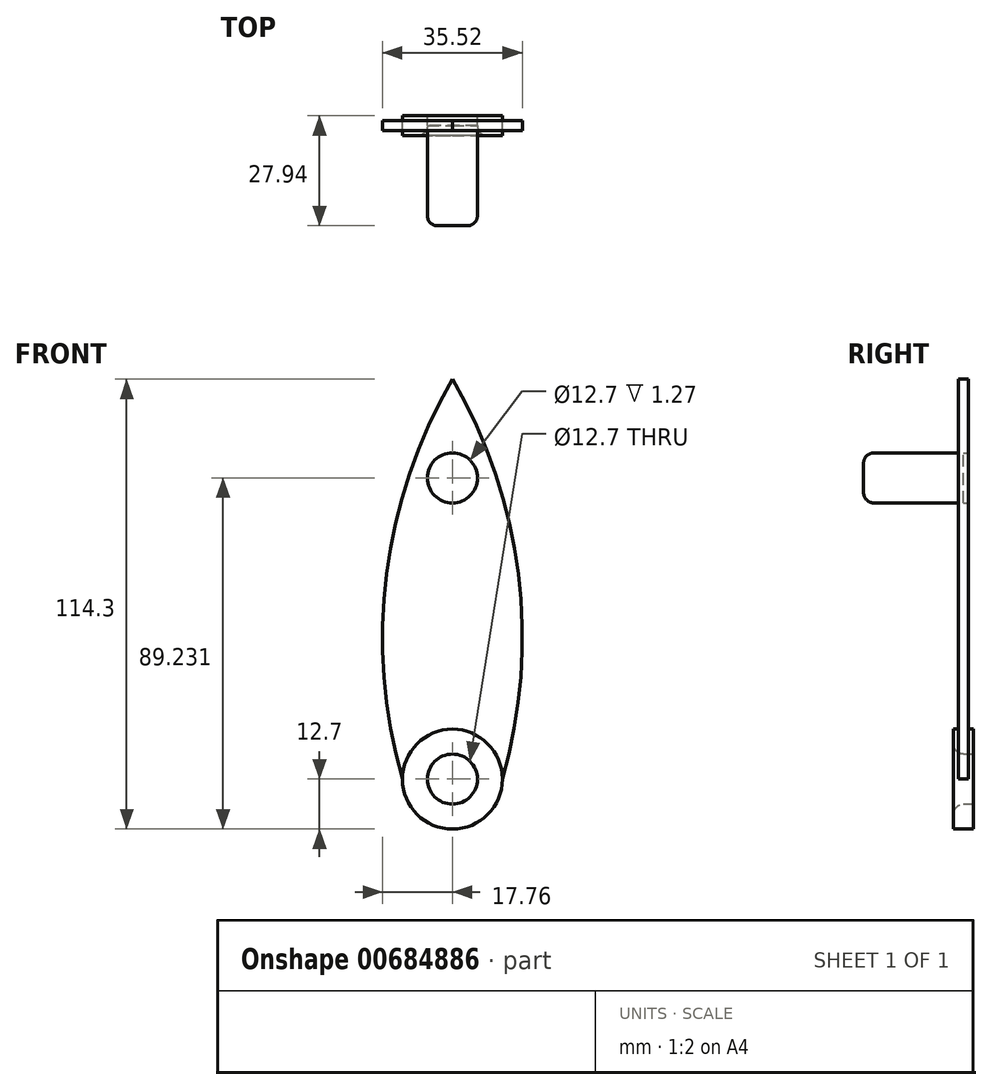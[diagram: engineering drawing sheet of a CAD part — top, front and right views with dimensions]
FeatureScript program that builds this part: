
annotation { "Feature Type Name" : "Feature", "Feature Type Description" : "" }
export const myFeature = defineFeature(function(context is Context, id is Id, definition is map)
    precondition{}
    {
        {
            var Q0;
            Q0=qCreatedBy(makeId("Front.planeOp"),FACE);
            var sketch = newSketch(context, id + "F0", { "sketchPlane" : qUnion([Q0])});
            skCircle(sketch, "E0", {"center": v(0, 0) * mm, "radius": 12.7 * mm});
            skCircle(sketch, "E1", {"center": v(0, 0) * mm, "radius": 6.35 * mm});
            skArc(sketch, "E2", {"start": v(0, 101.6) * mm, "mid": v(-16.75, 52.1) * mm, "end": v(-12.7, 0) * mm});
            skArc(sketch, "E3.MirrorCS", {"start": v(0, 101.6) * mm, "mid": v(16.75, 52.1) * mm, "end": v(12.7, 0) * mm});
            skCircle(sketch, "E4", {"center": v(0, 76.53) * mm, "radius": 6.35 * mm});
            skSolve(sketch);
        }
        {
            var Q0;
            Q0=makeQuery(id+"F0.imprint","IMPRINT",FACE,{"disambiguationData":[TD([[makeQuery(id+"F0.imprint","IMPRINT",EDGE,{"derivedFrom":sQuery(id+"F0.wireOp",EDGE,"E1")}),-1.0]])]});
            extrude(context, id + "F1", {"entities" : qUnion([Q0]), "endBound" : BoundingType.SYMMETRIC, "depth" : 5.08 * mm, "offsetDistance" : 25.4 * mm});
        }
        {
            var Q0;
            {var subQ0=sQuery(id+"F0.wireOp",EDGE,"E2");Q0=makeQuery(id+"F0.imprint","IMPRINT",FACE,{"disambiguationData":[TD([[makeQuery(id+"F0.imprint","IMPRINT",EDGE,{"derivedFrom":subQ0}),1.0]])]});}
            extrude(context, id + "F2", {"entities" : qUnion([Q0]), "operationType" : NewBodyOperationType.ADD, "endBound" : BoundingType.SYMMETRIC, "depth" : 2.54 * mm, "offsetDistance" : 25.4 * mm});
        }
        {
            var Q0;
            Q0=makeQuery(id+"F0.imprint","IMPRINT",FACE,{"disambiguationData":[TD([[makeQuery(id+"F0.imprint","IMPRINT",EDGE,{"derivedFrom":sQuery(id+"F0.wireOp",EDGE,"E4")}),1.0]])]});
            extrude(context, id + "F3", {"entities" : qUnion([Q0]), "operationType" : NewBodyOperationType.ADD, "depth" : 25.4 * mm, "offsetDistance" : 25.4 * mm});
        }
        {
            var Q0;
            Q0=makeQuery(id+"F3.opExtrude","CAP_EDGE",EDGE,{"disambiguationData":[OSD([sQuery(id+"F0.wireOp",EDGE,"E4")])],"isStart":false});
            var Q1;
            Q1=makeQuery(id+"F2.opExtrude","CAP_EDGE",EDGE,{"disambiguationData":[OSD([sQuery(id+"F0.wireOp",EDGE,"E4")])],"isStart":false});
            var Q2;
            Q2=makeQuery(id+"F1.opExtrude","CAP_EDGE",EDGE,{"disambiguationData":[OSD([sQuery(id+"F0.wireOp",EDGE,"E1")])],"isStart":false});
            var Q3;
            Q3=makeQuery(id+"F2.opExtrude","CAP_EDGE",EDGE,{"disambiguationData":[OSD([sQuery(id+"F0.wireOp",EDGE,"E0")])],"isStart":false});
            var Q4;
            Q4=makeQuery(id+"F2.opExtrude","CAP_EDGE",EDGE,{"disambiguationData":[OSD([sQuery(id+"F0.wireOp",EDGE,"E0")])],"isStart":true});
            fillet(context, id + "F4", {"entities" : qUnion([Q0, Q1, Q2, Q3, Q4]), "radius" : 2.54 * mm, "tangentPropagation" : true, "allowEdgeOverflow" : false});
        }
    });
